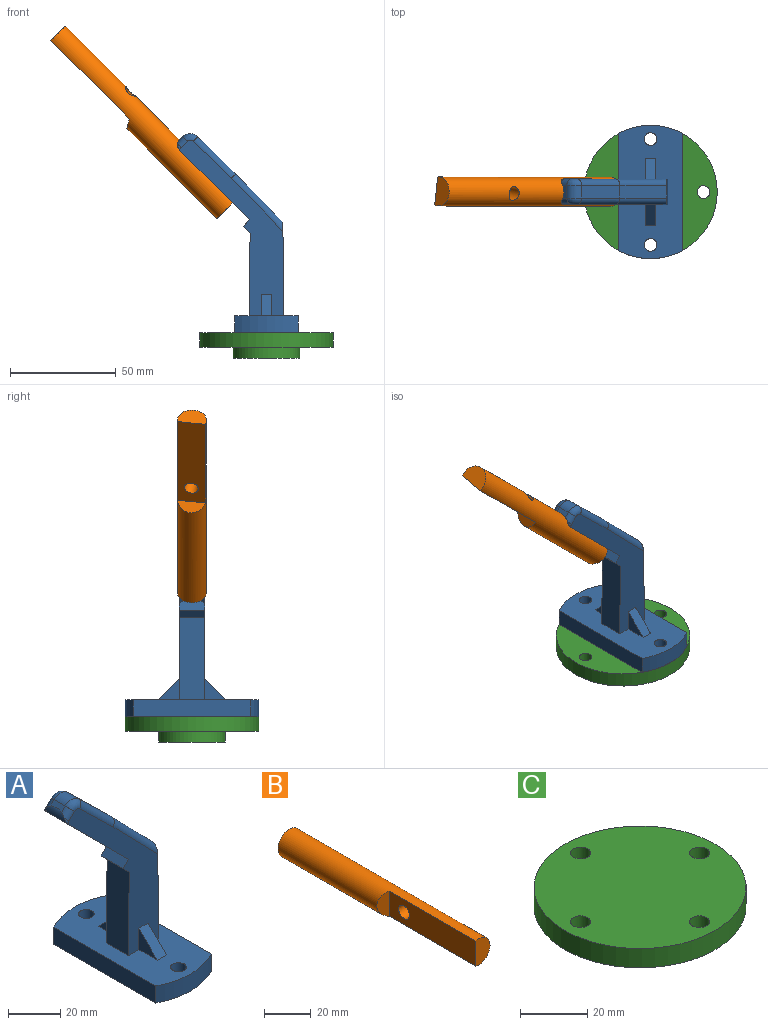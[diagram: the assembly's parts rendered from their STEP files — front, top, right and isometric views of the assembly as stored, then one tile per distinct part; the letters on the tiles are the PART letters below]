
ASSEMBLY  parts=3 mates=2
PART A: 35 faces, bbox 58.5x63x93.9 mm
  f0: plane 12x3.37mm, normal (-0.72,0,-0.7), area 56.5mm2, adj f2,f3,f5,f24
  f1: plane 18.06x17.61mm, normal (0.7,0,0.72), area 151.3mm2, adj f20,f22,f26,f31
  f2: plane 38.9x12mm, normal (-1,0,0.01), area 466.8mm2, adj f0,f3,f5,f6
  f3: plane 82.93x49.17mm, normal (0,-1,0), area 1055.3mm2, adj f0,f2,f4,f6,f14,f15,f16,f23
  f4: plane 44.18x12mm, normal (1,0,0.01), area 524.6mm2, adj f3,f5,f6,f22,f25,f30
  f5: plane 82.93x49.17mm, normal (0,1,0), area 1055.3mm2, adj f0,f2,f4,f6,f17,f18,f19,f23
  f6: plane 63x30mm, normal (0,0,1), area 1461.6mm2, adj f2,f3,f4,f5,f7,f8,f9,f10
  f7: plane 55.4x8mm, normal (1,0,0), area 443.2mm2, adj f6,f8,f12,f13
  f8: cylinder r=31.5mm len=30mm, axis (0,0,-1), area 250.1mm2, adj f6,f7,f9,f13
  f9: plane 55.4x8mm, normal (-1,0,0), area 443.2mm2, adj f6,f8,f12,f13
  f10: cylinder r=3mm len=8mm, axis (0,0,-1), area 150.8mm2, adj f6,f13
  f11: cylinder r=3mm len=8mm, axis (0,0,-1), area 150.8mm2, adj f6,f13
  f12: cylinder r=31.5mm len=30mm, axis (0,0,-1), area 250.1mm2, adj f6,f7,f9,f13
  f13: plane 63x30mm, normal (0,0,-1), area 1759.4mm2, adj f7,f8,f9,f10,f11,f12
  f14: plane 10x10mm, normal (-1,0,0), area 50mm2, adj f3,f6,f16
  f15: plane 10x10mm, normal (1,0,0), area 50mm2, adj f3,f6,f16
  f16: plane 10x10mm, normal (0,-0.71,0.71), area 70.7mm2, adj f3,f6,f14,f15
  f17: plane 10x10mm, normal (1,0,0), area 50mm2, adj f5,f6,f19
  f18: plane 10x10mm, normal (-1,0,0), area 50mm2, adj f5,f6,f19
  f19: plane 10x10mm, normal (0,0.71,0.71), area 70.7mm2, adj f5,f6,f17,f18
  f20: cylinder r=5mm len=7.03mm, axis (0,-1,0), area 46.8mm2, adj f1,f21,f27,f32
  f21: plane 6x1.98mm, normal (-0.71,0,0.71), area 14.1mm2, adj f20,f23,f28,f33
  f22: plane 22.72x22.16mm, normal (0.72,0,0.7), area 190.4mm2, adj f1,f4,f25,f30
  f23: cylinder r=7mm len=37.76mm, axis (-0.71,0,0.71), area 714.2mm2, adj f3,f5,f21,f24,f28,f29,f33,f34
  f24: plane 12x5.34mm, normal (-0.71,0,0.71), area 78.8mm2, adj f0,f3,f5,f23
  f25: cylinder r=3mm len=27.07mm, axis (0.7,0,-0.72), area 154.9mm2, adj f4,f5,f22,f26
  f26: cylinder r=3mm len=20.15mm, axis (0.72,0,-0.7), area 118.8mm2, adj f1,f5,f25,f27
  f27: torus R=2mm, axis (0,-1,0), area 28.7mm2, adj f5,f20,f26,f28
  f28: cylinder r=3mm len=5.04mm, axis (0.71,0,0.71), area 18.1mm2, adj f5,f21,f23,f27,f29
  f29: torus R=2mm, axis (0,-1,0), area 2.4mm2, adj f5,f23,f28
  f30: cylinder r=3mm len=27.07mm, axis (-0.7,0,0.72), area 154.9mm2, adj f3,f4,f22,f31
  f31: cylinder r=3mm len=20.15mm, axis (-0.72,0,0.7), area 118.8mm2, adj f1,f3,f30,f32
  f32: torus R=2mm, axis (0,-1,0), area 28.7mm2, adj f3,f20,f31,f33
  f33: cylinder r=3mm len=5.04mm, axis (-0.71,0,-0.71), area 18.1mm2, adj f3,f21,f23,f32,f34
  f34: torus R=2mm, axis (0,-1,0), area 2.4mm2, adj f3,f23,f33
PART B: 6 faces, bbox 13.7x115x13.7 mm
  f0: cylinder r=6.85mm len=115mm, axis (0,1,0), area 3952.5mm2, adj f1,f2,f3,f4,f5
  f1: plane 13.7x8.7mm, normal (0,-1,0), area 98.7mm2, adj f0,f4
  f2: plane 13.7x13.7mm, normal (0,1,0), area 147.4mm2, adj f0
  f3: plane 13.19x5mm, normal (-0.45,-0.89,0), area 54.4mm2, adj f0,f4
  f4: plane 52.5x13.19mm, normal (-1,0,0), area 658.3mm2, adj f0,f1,f3,f5
  f5: cylinder r=3.3mm len=8.7mm, axis (-1,0,0), area 171.8mm2, adj f0,f4
PART C: 9 faces, bbox 63x63x12 mm
  f0: plane 63x63mm, normal (0,0,-1), area 2224.8mm2, adj f2,f3,f4,f5,f6,f7
  f1: plane 63x63mm, normal (0,0,1), area 3004.1mm2, adj f2,f3,f4,f5,f6
  f2: cylinder r=31.5mm len=63mm, axis (0,0,1), area 1385.4mm2, adj f0,f1
  f3: cylinder r=3mm len=7mm, axis (0,0,1), area 131.9mm2, adj f0,f1
  f4: cylinder r=3mm len=7mm, axis (0,0,1), area 131.9mm2, adj f0,f1
  f5: cylinder r=3mm len=7mm, axis (0,0,1), area 131.9mm2, adj f0,f1
  f6: cylinder r=3mm len=7mm, axis (0,0,1), area 131.9mm2, adj f0,f1
  f7: cylinder r=15.75mm len=31.5mm, axis (0,0,1), area 494.8mm2, adj f0,f8
  f8: plane 31.5x31.5mm, normal (0,0,-1), area 779.3mm2, adj f7
PLACE A t=(0.33,-5.2,31.52)mm
PLACE B rot(axis=(-0.85,-0.3,-0.43),95.7deg) t=(-60.7,-5.2,132.56)mm
PLACE C t=(0.33,-5.2,31.52)mm fixed
MATE fastened A.f8 <-> C.f2  axis (0,0,-1) through (0.33,-5.2,31.52)mm
MATE cylindrical B.f0 <-> A.f23  axis (0.71,0,-0.71) through (-18.27,-5.2,90.14)mm
